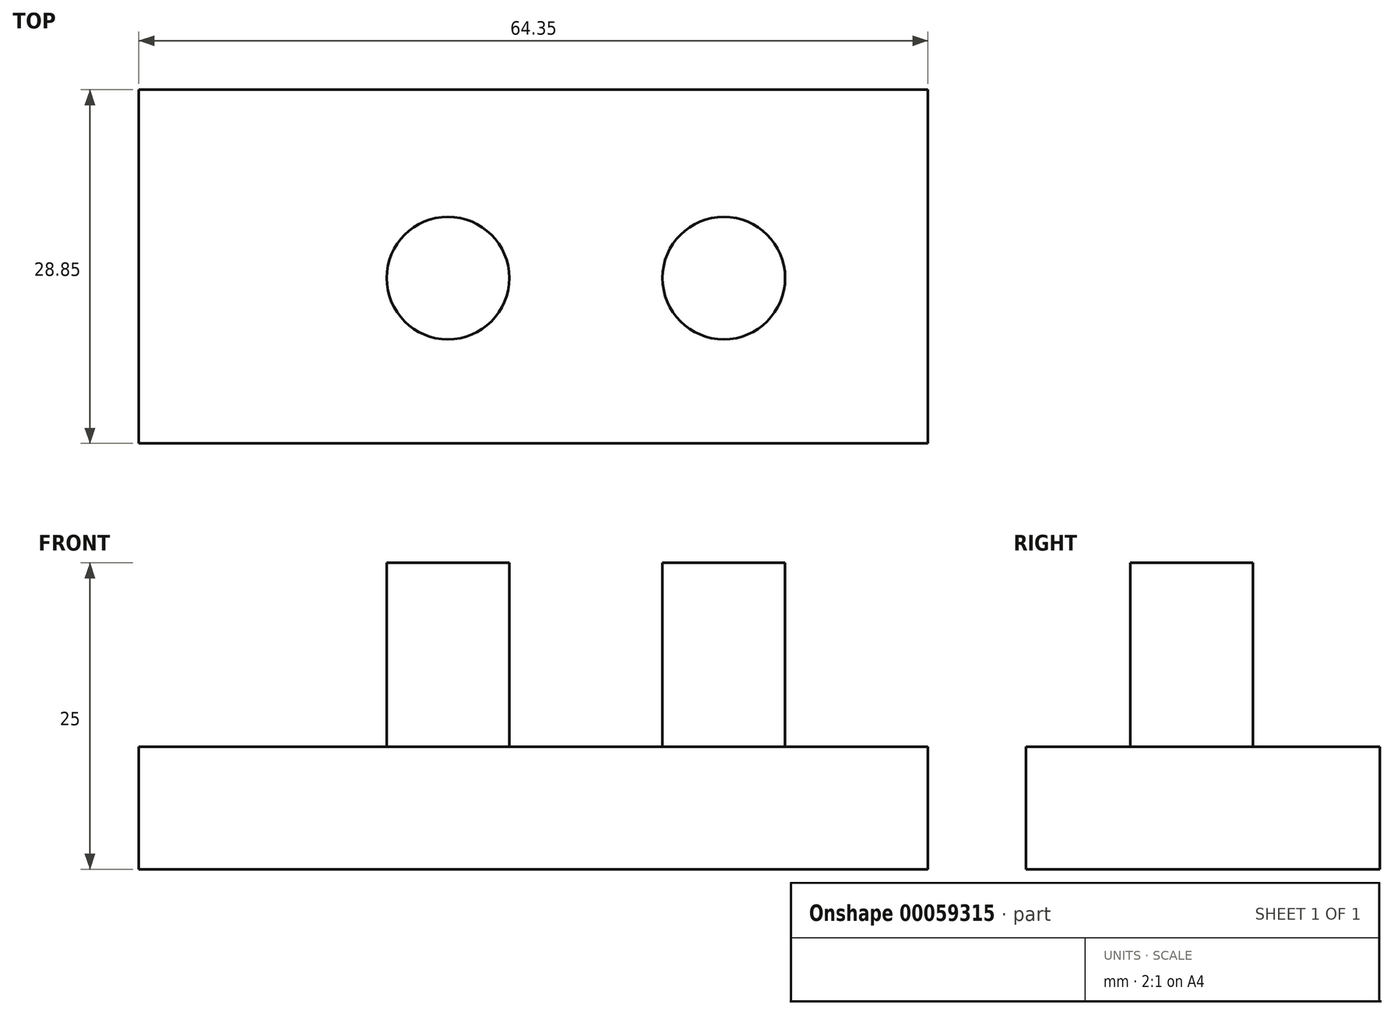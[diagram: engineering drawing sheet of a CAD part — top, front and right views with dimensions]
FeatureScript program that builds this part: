
annotation { "Feature Type Name" : "Feature", "Feature Type Description" : "" }
export const myFeature = defineFeature(function(context is Context, id is Id, definition is map)
    precondition{}
    {
        {
            var Q0;
            Q0=qCreatedBy(makeId("Top.planeOp"),FACE);
            var sketch = newSketch(context, id + "F0", { "sketchPlane" : qUnion([Q0])});
            skCircle(sketch, "E0", {"center": v(0, 0) * mm, "radius": 5 * mm});
            skLineSegment(sketch, "E1.bottom", {"start": v(-25.2, 15.36) * mm, "end": v(39.15, 15.36) * mm});
            skLineSegment(sketch, "E1.top", {"start": v(-25.2, -13.5) * mm, "end": v(39.15, -13.5) * mm});
            skLineSegment(sketch, "E1.left", {"start": v(-25.2, 15.36) * mm, "end": v(-25.2, -13.5) * mm});
            skLineSegment(sketch, "E1.right", {"start": v(39.15, 15.36) * mm, "end": v(39.15, -13.5) * mm});
            skCircle(sketch, "E2", {"center": v(30.75, 0) * mm, "radius": 5 * mm});
            skSolve(sketch);
        }
        {
            var Q0;
            Q0=makeQuery(id+"F0.imprint","IMPRINT",FACE,{"disambiguationData":[TD([[makeQuery(id+"F0.imprint","IMPRINT",EDGE,{"derivedFrom":sQuery(id+"F0.wireOp",EDGE,"E0")}),-1.0]])]});
            var Q1;
            Q1=makeQuery(id+"F0.imprint","IMPRINT",FACE,{"disambiguationData":[TD([[makeQuery(id+"F0.imprint","IMPRINT",EDGE,{"derivedFrom":sQuery(id+"F0.wireOp",EDGE,"E0")}),1.0]])]});
            var Q2;
            Q2=makeQuery(id+"F0.imprint","IMPRINT",FACE,{"disambiguationData":[TD([[makeQuery(id+"F0.imprint","IMPRINT",EDGE,{"derivedFrom":sQuery(id+"F0.wireOp",EDGE,"E2")}),1.0]])]});
            extrude(context, id + "F1", {"entities" : qUnion([Q0, Q1, Q2]), "depth" : 10 * mm});
        }
        {
            var Q0;
            Q0=makeQuery(id+"F1.opExtrude","CAP_FACE",FACE,{"disambiguationData":[OSD([sQuery(id+"F0.wireOp",EDGE,"E1.bottom"),sQuery(id+"F0.wireOp",EDGE,"E1.top"),sQuery(id+"F0.wireOp",EDGE,"E1.left"),sQuery(id+"F0.wireOp",EDGE,"E1.right")])],"isStart":false});
            var sketch = newSketch(context, id + "F2", { "sketchPlane" : qUnion([Q0])});
            skCircle(sketch, "E3", {"center": v(0, 0) * mm, "radius": 5 * mm});
            skCircle(sketch, "E4", {"center": v(22.5, 0) * mm, "radius": 5 * mm});
            skSolve(sketch);
        }
        {
            var Q0;
            Q0=makeQuery(id+"F2.imprint","IMPRINT",FACE,{"disambiguationData":[TD([[makeQuery(id+"F2.imprint","IMPRINT",EDGE,{"derivedFrom":sQuery(id+"F2.wireOp",EDGE,"E3")}),1.0]])]});
            var Q1;
            Q1=makeQuery(id+"F2.imprint","IMPRINT",FACE,{"disambiguationData":[TD([[makeQuery(id+"F2.imprint","IMPRINT",EDGE,{"derivedFrom":sQuery(id+"F2.wireOp",EDGE,"E4")}),1.0]])]});
            extrude(context, id + "F3", {"entities" : qUnion([Q0, Q1]), "operationType" : NewBodyOperationType.ADD, "depth" : 15 * mm});
        }
    });
